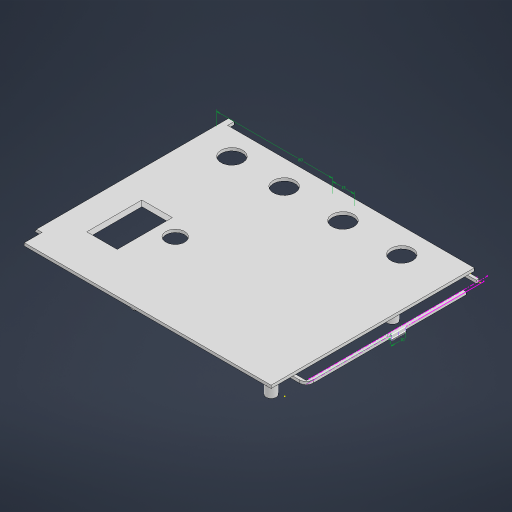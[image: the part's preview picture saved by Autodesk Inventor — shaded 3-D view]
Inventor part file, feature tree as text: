
AUTODESK INVENTOR PART (.ipt)
format: ipt  version: 2024.2 (Build 282272000, 272)  size: 350,720 bytes
history: native  units: mm
features: sketch x12, extrude x8, hole x4, chamfer x3, projected_geometry x3, fillet x1
ambient origin geometry x8: Origin, YZ Plane, XZ Plane, XY Plane, X Axis, Y Axis, Z Axis, Center Point
bodies: Volumenkörper1 (feature_tree)
feature tree (31):
  extrude  "Extrusion1"  Depth=140.0mm
  chamfer  "Fase1"  Distance=48.5mm
  extrude  "Extrusion2"  Depth=2.0mm TaperAngle=0.0deg
  extrude  "Extrusion3"  Depth=2.0mm TaperAngle=45.0deg
  hole  "Bohrung1"  [1 undecoded]
  hole  "Bohrung2"  [1 undecoded]
  hole  "Bohrung3"  [1 undecoded]
  hole  "Bohrung4"  [1 undecoded]
  extrude  "Extrusion4"  Depth=3.5mm
  extrude  "Extrusion5"  Depth=3.5mm
  fillet  "Rundung1"  Radius=7.0mm
  sketch  "Skizze10"  dims[d13=30.0mm]
  extrude  "Extrusion6"  Depth=3.5mm
  extrude  "Extrusion7"  Depth=3.2mm
  chamfer  "Fase2"  Distance=87.0mm
  chamfer  "Fase3"  Distance=4.5mm
  extrude  "Extrusion8"  Depth=2.5mm TaperAngle=0.0deg
  sketch  "Skizze12"  dims[d15=13.0mm d17=48.5mm d18=2.0mm d19=0.0mm d20=2.0mm d21=2.0mm d22=45.0deg d23=7.0mm d24=7.0mm d25=7.0mm d26=3.5mm d28=3.5mm d29=3.5mm d30=7.0mm d31=3.5mm d32=87.0mm d33=87.0mm d34=4.5mm d35=0.0mm d36=2.5mm d37=0.0mm d38=3.0mm d39=6.0mm d40=4.0mm d41=2.0mm d42=90.0deg d43=5.0mm d44=0.0mm d45=3.0mm d46=6.0mm d47=4.0mm d48=2.0mm d49=90.0deg d50=7.0mm d51=0.0mm d52=3.0mm d53=6.0mm d54=4.0mm d55=2.0mm d56=90.0deg d57=7.0mm d58=0.0mm d59=3.0mm d60=6.0mm d61=4.0mm d62=2.0mm d63=90.0deg d64=5.0mm d65=0.0mm d66=25.0mm d67=25.0mm d68=2.0mm d69=0.0mm d70=2.7mm d71=2.7mm d72=0.0mm d73=2.7mm d74=2.0mm d75=2.0mm d76=2.0mm d77=2.0mm d78=2.0mm d79=0.0mm d80=4.75mm d81=127.739418mm d83=1.0mm d84=2.0mm d85=0.0mm d86=0.4mm d87=0.0mm d88=0.25mm d89=2.0mm d90=45.0deg d91=10.0mm d92=2.5mm d93=2.0mm d94=2.0mm d95=30.0deg d96=3.2mm d97=0.0mm d98=15.0mm d99=80.0mm d100=25.5mm]
  sketch  "Skizze1"  dims[d0=170.0mm d1=140.0mm]
  sketch  "Skizze2"  dims[d2=15.0mm]
  sketch  "Skizze3"  dims[d3=123.0mm]
  projected_geometry  "Projizierte Kontur1"
  projected_geometry  "Projizierte Kontur2"
  sketch  "Skizze4"  dims[d4=20.0mm]
  sketch  "Skizze5"  dims[d8=56.0mm]
  sketch  "Skizze6"  dims[d9=96.5mm]
  sketch  "Skizze7"  dims[d10=137.0mm]
  projected_geometry  "Projizierte Kontur3"
  sketch  "Skizze8"  dims[d11=17.0mm]
  sketch  "Skizze9"  dims[d12=34.0mm]
  sketch  "Skizze11"  dims[d14=17.0mm]
note: 4 required parameter values undecoded (feature->parameter linkage not recoverable at this tier; creation-order binding heuristic only, values carry confidence <= 0.55)
